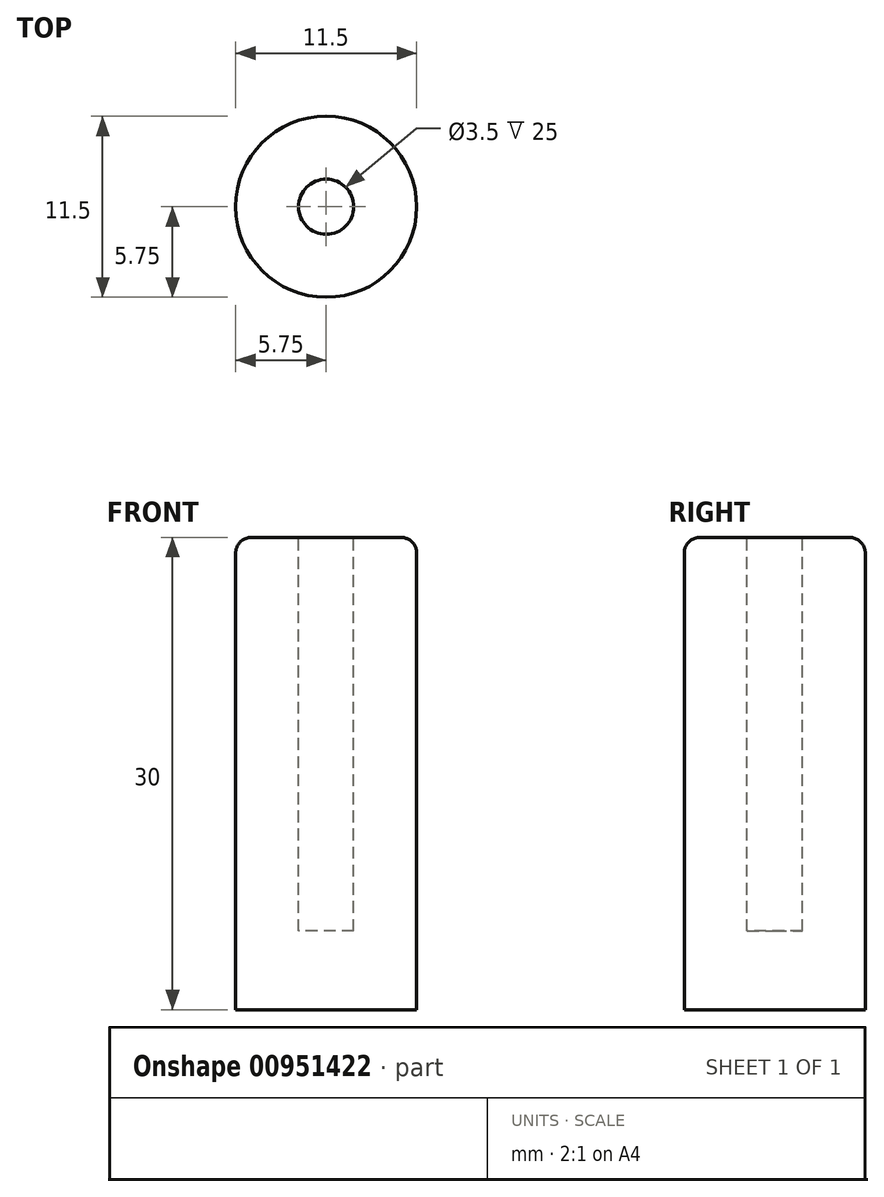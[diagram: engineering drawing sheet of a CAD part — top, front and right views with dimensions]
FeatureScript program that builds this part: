
annotation { "Feature Type Name" : "Feature", "Feature Type Description" : "" }
export const myFeature = defineFeature(function(context is Context, id is Id, definition is map)
    precondition{}
    {
        {
            var Q0;
            Q0=qCreatedBy(makeId("Top.planeOp"),FACE);
            var sketch = newSketch(context, id + "F0", { "sketchPlane" : qUnion([Q0])});
            skCircle(sketch, "E0", {"center": v(0, 0) * mm, "radius": 5.75 * mm});
            skSolve(sketch);
        }
        {
            var Q0;
            Q0 = qSketchRegion(id + "F0", true);
            extrude(context, id + "F1", {"entities" : qUnion([Q0]), "depth" : 30 * mm, "offsetDistance" : 25 * mm});
        }
        {
            var Q0;
            Q0=makeQuery(id+"F1.opExtrude","CAP_FACE",FACE,{"disambiguationData":[OSD([sQuery(id+"F0.wireOp",EDGE,"E0")])],"isStart":false});
            var sketch = newSketch(context, id + "F2", { "sketchPlane" : qUnion([Q0])});
            skCircle(sketch, "E1", {"center": v(0, 0) * mm, "radius": 1.75 * mm});
            skSolve(sketch);
        }
        {
            var Q0;
            Q0=makeQuery(id+"F2.imprint","IMPRINT",FACE,{"disambiguationData":[TD([[makeQuery(id+"F2.imprint","IMPRINT",EDGE,{"derivedFrom":sQuery(id+"F2.wireOp",EDGE,"E1")}),1.0]])]});
            extrude(context, id + "F3", {"entities" : qUnion([Q0]), "operationType" : NewBodyOperationType.REMOVE, "oppositeDirection" : true, "depth" : 25 * mm, "offsetDistance" : 25 * mm});
        }
        {
            var Q0;
            Q0=makeQuery(id+"F1.opExtrude","CAP_EDGE",EDGE,{"disambiguationData":[OSD([sQuery(id+"F0.wireOp",EDGE,"E0")])],"isStart":false});
            fillet(context, id + "F4", {"entities" : qUnion([Q0]), "radius" : 1 * mm, "tangentPropagation" : true, "allowEdgeOverflow" : false});
        }
    });
